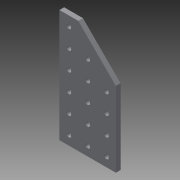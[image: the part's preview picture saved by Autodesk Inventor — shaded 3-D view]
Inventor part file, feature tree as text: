
AUTODESK INVENTOR PART (.ipt)
format: ipt  version: 2013 (Build 170138000, 138)  size: 94,208 bytes
history: native  units: in
note: dims shown in document units (in); Inventor stores cm internally (conversion verified against a paired STEP export)
features: extrude x1, sketch x1
ambient origin geometry x8: Origin, YZ Plane, XZ Plane, XY Plane, X Axis, Y Axis, Z Axis, Center Point
bodies: Solid1 (feature_tree)
feature tree (2):
  extrude  "Extrusion1"  [1 undecoded]
  sketch  "Sketch2"  dims[d1=0.1969in d2=0.0in]
note: 1 required parameter value undecoded (feature->parameter linkage not recoverable at this tier; creation-order binding heuristic only, values carry confidence <= 0.55)
